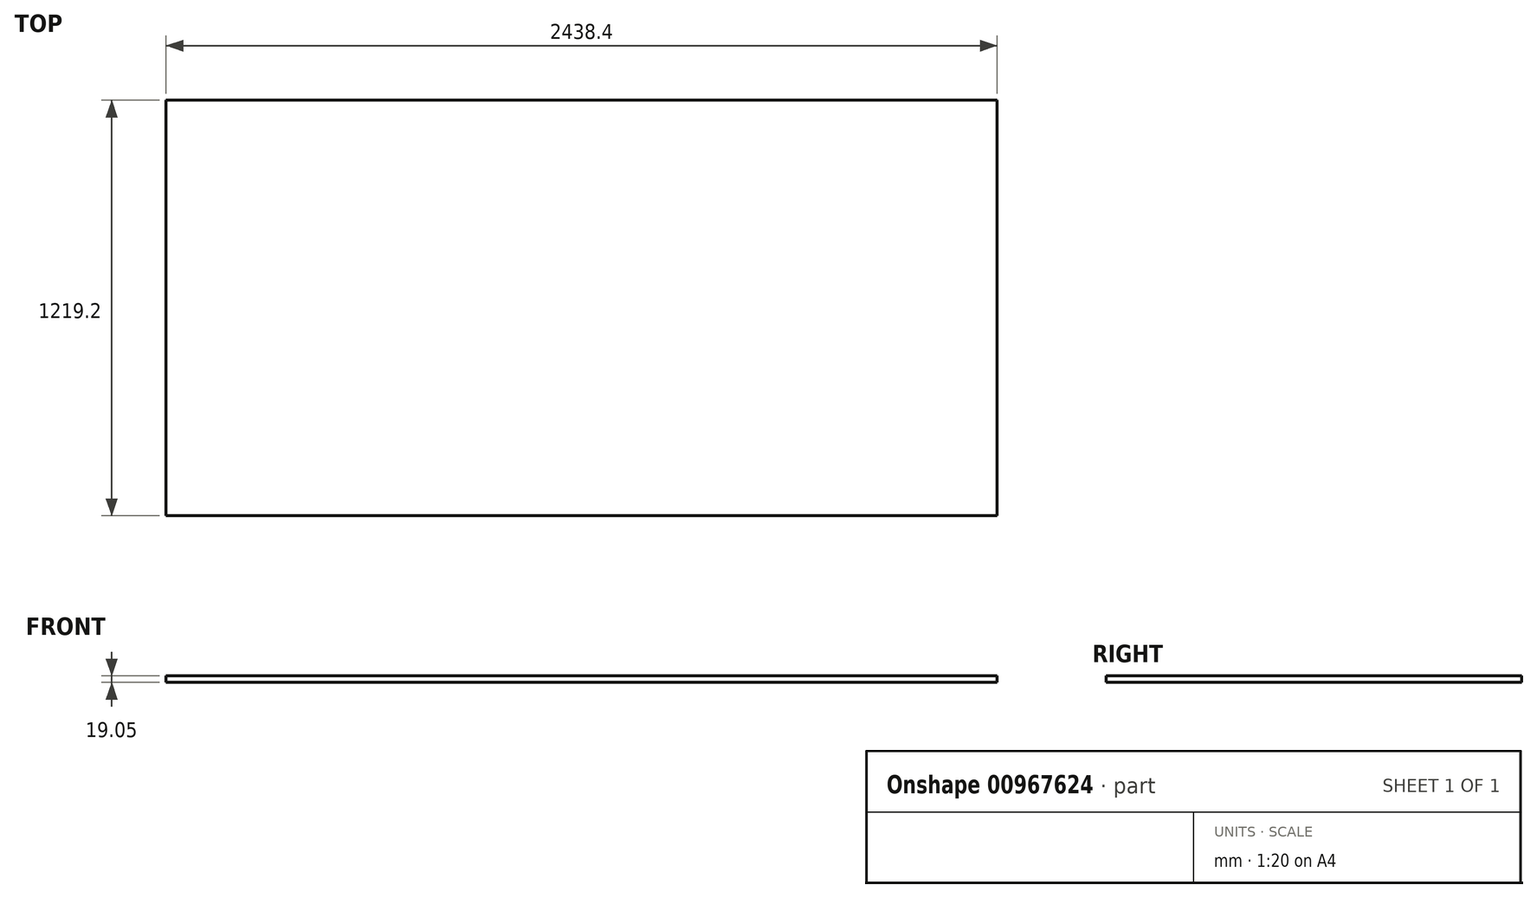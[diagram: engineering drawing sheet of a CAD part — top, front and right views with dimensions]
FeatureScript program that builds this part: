
annotation { "Feature Type Name" : "Feature", "Feature Type Description" : "" }
export const myFeature = defineFeature(function(context is Context, id is Id, definition is map)
    precondition{}
    {
        {
            var Q0;
            Q0=qCreatedBy(makeId("Top.planeOp"),FACE);
            var sketch = newSketch(context, id + "F0", { "sketchPlane" : qUnion([Q0])});
            skLineSegment(sketch, "E0.bottom", {"start": v(0, 0) * mm, "end": v(2438.4, 0) * mm});
            skLineSegment(sketch, "E0.top", {"start": v(0, 1219.2) * mm, "end": v(2438.4, 1219.2) * mm});
            skLineSegment(sketch, "E0.left", {"start": v(0, 0) * mm, "end": v(0, 1219.2) * mm});
            skLineSegment(sketch, "E0.right", {"start": v(2438.4, 0) * mm, "end": v(2438.4, 1219.2) * mm});
            skSolve(sketch);
        }
        {
            var Q0;
            Q0 = qSketchRegion(id + "F0", true);
            extrude(context, id + "F1", {"entities" : qUnion([Q0]), "depth" : 19.05 * mm, "offsetDistance" : 25.4 * mm});
        }
    });
